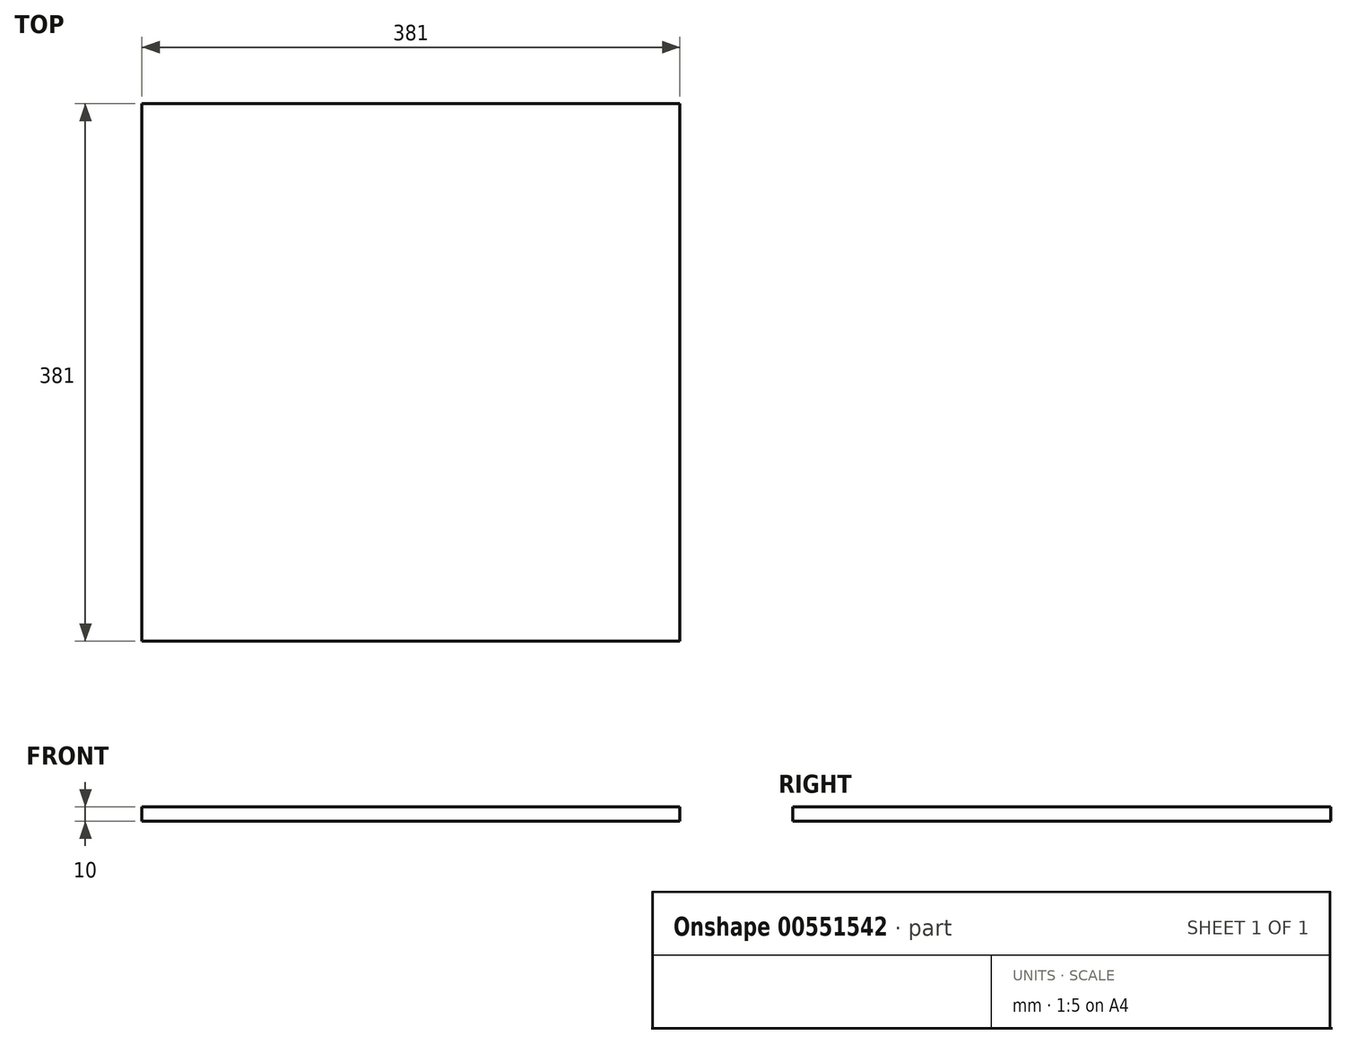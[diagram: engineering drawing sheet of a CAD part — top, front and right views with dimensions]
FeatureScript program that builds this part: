
annotation { "Feature Type Name" : "Feature", "Feature Type Description" : "" }
export const myFeature = defineFeature(function(context is Context, id is Id, definition is map)
    precondition{}
    {
        {
            var Q0;
            Q0=qCreatedBy(makeId("Top.planeOp"),FACE);
            var sketch = newSketch(context, id + "F0", { "sketchPlane" : qUnion([Q0])});
            skLineSegment(sketch, "E0.bottom", {"start": v(-185.24, 247.29) * mm, "end": v(195.76, 247.29) * mm});
            skLineSegment(sketch, "E0.top", {"start": v(-185.24, -133.71) * mm, "end": v(195.76, -133.71) * mm});
            skLineSegment(sketch, "E0.left", {"start": v(-185.24, 247.29) * mm, "end": v(-185.24, -133.71) * mm});
            skLineSegment(sketch, "E0.right", {"start": v(195.76, 247.29) * mm, "end": v(195.76, -133.71) * mm});
            skSolve(sketch);
        }
        {
            var Q0;
            Q0=makeQuery(id+"F0.imprint","IMPRINT",FACE,{"disambiguationData":[TD([[makeQuery(id+"F0.imprint","IMPRINT",EDGE,{"derivedFrom":sQuery(id+"F0.wireOp",EDGE,"E0.bottom")}),-1.0]])]});
            extrude(context, id + "F1", {"entities" : qUnion([Q0]), "depth" : 10 * mm, "offsetDistance" : 25 * mm});
        }
    });
